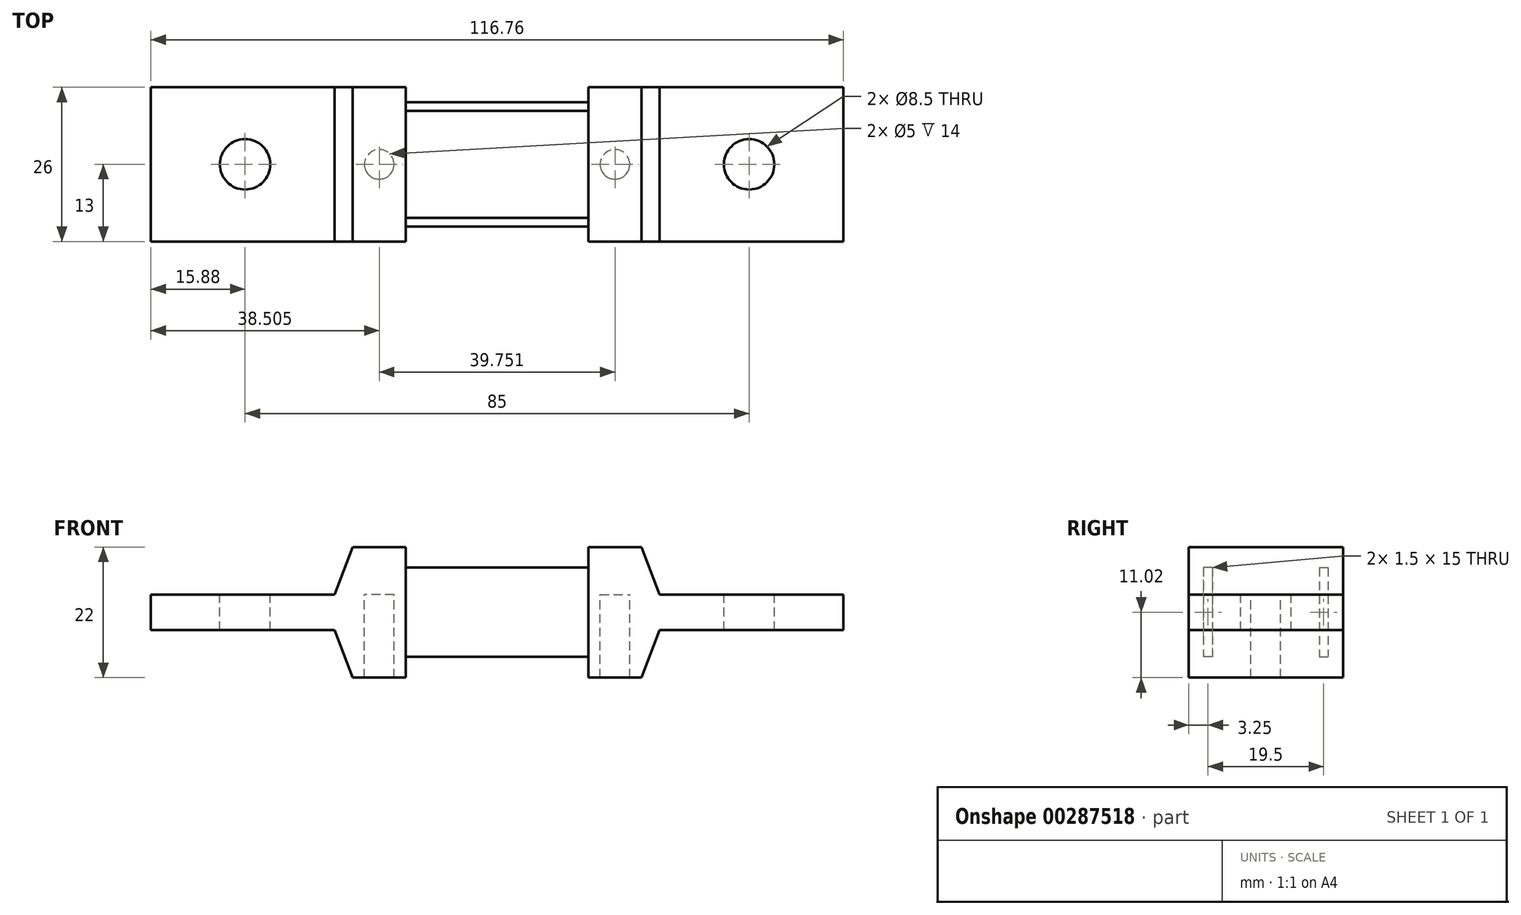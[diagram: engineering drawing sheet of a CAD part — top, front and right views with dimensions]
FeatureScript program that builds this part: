
annotation { "Feature Type Name" : "Feature", "Feature Type Description" : "" }
export const myFeature = defineFeature(function(context is Context, id is Id, definition is map)
    precondition{}
    {
        {
            var Q0;
            Q0=qCreatedBy(makeId("Front.planeOp"),FACE);
            var sketch = newSketch(context, id + "F0", { "sketchPlane" : qUnion([Q0])});
            skPoint(sketch, "E0.middle", {"position": v(0, 0) * mm});
            skLineSegment(sketch, "E1.bottom", {"start": v(15.38, -8.88) * mm, "end": v(-15.38, -8.88) * mm});
            skLineSegment(sketch, "E1.top", {"start": v(15.38, 8.88) * mm, "end": v(-15.38, 8.88) * mm});
            skLineSegment(sketch, "E1.left", {"start": v(15.38, -8.88) * mm, "end": v(15.38, 8.88) * mm});
            skLineSegment(sketch, "E1.right", {"start": v(-15.38, -8.88) * mm, "end": v(-15.38, 8.88) * mm});
            skLineSegment(sketch, "E2", {"start": v(-58.38, -3.02) * mm, "end": v(-27.38, -3.02) * mm});
            skLineSegment(sketch, "E3", {"start": v(-27.38, -3.02) * mm, "end": v(-24.38, -11.02) * mm});
            skLineSegment(sketch, "E4", {"start": v(-24.38, -11.02) * mm, "end": v(-15.38, -11.02) * mm});
            skLineSegment(sketch, "E5", {"start": v(-15.38, -11.02) * mm, "end": v(-15.38, 10.98) * mm});
            skLineSegment(sketch, "E6", {"start": v(-15.38, 10.98) * mm, "end": v(-24.38, 10.98) * mm});
            skLineSegment(sketch, "E7", {"start": v(-24.38, 10.98) * mm, "end": v(-27.38, 2.98) * mm});
            skLineSegment(sketch, "E8", {"start": v(-27.38, 2.98) * mm, "end": v(-58.38, 2.98) * mm});
            skLineSegment(sketch, "E9", {"start": v(-58.38, 2.98) * mm, "end": v(-58.38, -3.02) * mm});
            skSolve(sketch);
        }
        {
            var Q0;
            Q0=makeQuery(id+"F0.imprint","IMPRINT",FACE,{"disambiguationData":[TD([[makeQuery(id+"F0.imprint","IMPRINT",EDGE,{"derivedFrom":sQuery(id+"F0.wireOp",EDGE,"E2")}),1.0]])]});
            extrude(context, id + "F1", {"entities" : qUnion([Q0]), "endBound" : BoundingType.SYMMETRIC, "oppositeDirection" : true, "depth" : 26 * mm});
        }
        {
            var Q0;
            Q0=makeQuery(id+"F1.opExtrude","SWEPT_FACE",FACE,{"disambiguationData":[OSD([sQuery(id+"F0.wireOp",EDGE,"E8")])]});
            var sketch = newSketch(context, id + "F2", { "sketchPlane" : qUnion([Q0])});
            skCircle(sketch, "E10", {"center": v(-42.5, 0) * mm, "radius": 4.25 * mm});
            skCircle(sketch, "E11", {"center": v(-19.88, 0) * mm, "radius": 2.5 * mm});
            skSolve(sketch);
        }
        {
            var Q0;
            Q0 = qSketchRegion(id + "F2", true);
            var Q1;
            Q1=makeQuery(id+"F1.opExtrude","SWEPT_FACE",FACE,{"disambiguationData":[OSD([sQuery(id+"F0.wireOp",EDGE,"E4")])]});
            extrude(context, id + "F3", {"entities" : qUnion([Q0]), "operationType" : NewBodyOperationType.REMOVE, "endBound" : BoundingType.UP_TO_SURFACE, "oppositeDirection" : true, "endBoundEntityFace" : qUnion([Q1]), "depth" : 25 * mm});
        }
        {
            var Q0;
            Q0=makeQuery(id+"F1.opExtrude","SWEPT_BODY",BODY,{"disambiguationData":[OSD([sQuery(id+"F0.wireOp",EDGE,"E2"),sQuery(id+"F0.wireOp",EDGE,"E3"),sQuery(id+"F0.wireOp",EDGE,"E4"),sQuery(id+"F0.wireOp",EDGE,"E5"),sQuery(id+"F0.wireOp",EDGE,"E6"),sQuery(id+"F0.wireOp",EDGE,"E7"),sQuery(id+"F0.wireOp",EDGE,"E8"),sQuery(id+"F0.wireOp",EDGE,"E9")])]});
            var Q1;
            Q1=qCreatedBy(makeId("Right.planeOp"),FACE);
            mirror(context, id + "F4", {"entities" : qUnion([Q0]), "mirrorPlane" : qUnion([Q1])});
        }
        {
            var Q0;
            Q0=qCreatedBy(makeId("Top.planeOp"),FACE);
            var sketch = newSketch(context, id + "F5", { "sketchPlane" : qUnion([Q0])});
            skLineSegment(sketch, "E12.bottom", {"start": v(15.38, 9) * mm, "end": v(-15.38, 9) * mm});
            skLineSegment(sketch, "E12.top", {"start": v(15.38, 10.5) * mm, "end": v(-15.38, 10.5) * mm});
            skLineSegment(sketch, "E12.left", {"start": v(15.38, 9) * mm, "end": v(15.38, 10.5) * mm});
            skLineSegment(sketch, "E12.right", {"start": v(-15.38, 9) * mm, "end": v(-15.38, 10.5) * mm});
            skPoint(sketch, "E12.middle", {"position": v(0, 9.75) * mm});
            skLineSegment(sketch, "E13", {"start": v(0, 0) * mm, "end": v(-12.63, 0) * mm, "construction": true});
            skLineSegment(sketch, "E14.MirrorCS", {"start": v(15.38, -9) * mm, "end": v(15.38, -10.5) * mm});
            skLineSegment(sketch, "E15.MirrorCS", {"start": v(-15.38, -9) * mm, "end": v(-15.38, -10.5) * mm});
            skLineSegment(sketch, "E16.MirrorCS", {"start": v(15.38, -9) * mm, "end": v(-15.38, -9) * mm});
            skLineSegment(sketch, "E17.MirrorCS", {"start": v(15.38, -10.5) * mm, "end": v(-15.38, -10.5) * mm});
            skPoint(sketch, "E18.MirrorP", {"position": v(0, -9.75) * mm});
            skSolve(sketch);
        }
        {
            var Q0;
            Q0 = qSketchRegion(id + "F5", true);
            extrude(context, id + "F6", {"entities" : qUnion([Q0]), "operationType" : NewBodyOperationType.ADD, "endBound" : BoundingType.SYMMETRIC, "depth" : 15 * mm});
        }
    });
